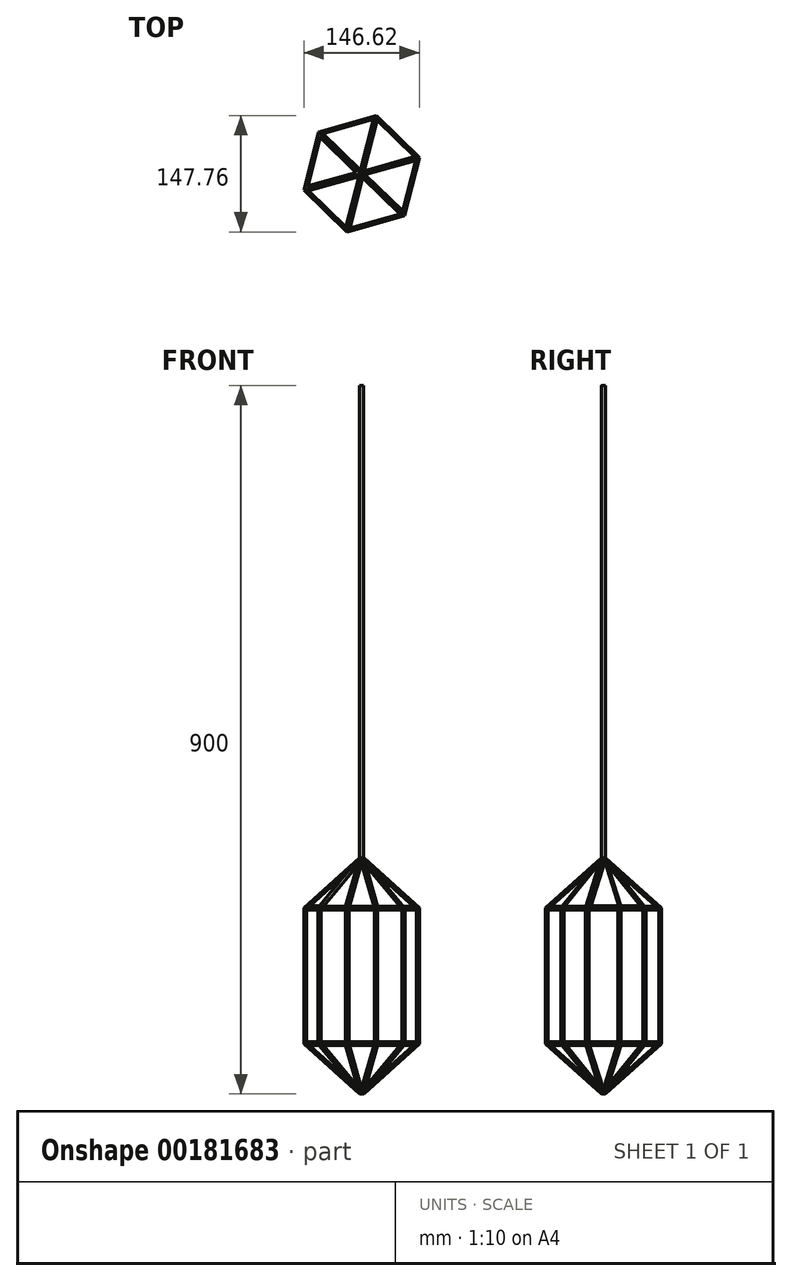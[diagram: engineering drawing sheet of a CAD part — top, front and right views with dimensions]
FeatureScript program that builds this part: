
annotation { "Feature Type Name" : "Feature", "Feature Type Description" : "" }
export const myFeature = defineFeature(function(context is Context, id is Id, definition is map)
    precondition{}
    {
        {
            var Q0;
            Q0=qCreatedBy(makeId("Top.planeOp"),FACE);
            var sketch = newSketch(context, id + "F0", { "sketchPlane" : qUnion([Q0])});
            skCircle(sketch, "E0.cCircle", {"center": v(0, 0) * mm, "radius": 66 * mm, "construction": true});
            skLineSegment(sketch, "E0.0", {"start": v(18.67, 73.88) * mm, "end": v(73.31, 20.77) * mm});
            skLineSegment(sketch, "E0.1", {"start": v(73.31, 20.77) * mm, "end": v(54.65, -53.1) * mm});
            skLineSegment(sketch, "E0.2", {"start": v(54.65, -53.1) * mm, "end": v(-18.67, -73.88) * mm});
            skLineSegment(sketch, "E0.3", {"start": v(-18.67, -73.88) * mm, "end": v(-73.31, -20.77) * mm});
            skLineSegment(sketch, "E0.4", {"start": v(-73.31, -20.77) * mm, "end": v(-54.65, 53.1) * mm});
            skLineSegment(sketch, "E0.5", {"start": v(-54.65, 53.1) * mm, "end": v(18.67, 73.88) * mm});
            skPoint(sketch, "E0.0.midPoint", {"position": v(45.99, 47.33) * mm});
            skSolve(sketch);
        }
        {
            var Q0;
            Q0 = qSketchRegion(id + "F0", true);
            extrude(context, id + "F1", {"entities" : qUnion([Q0]), "depth" : 300 * mm});
        }
        {
            var Q0;
            Q0=makeQuery(id+"F1.opExtrude","CAP_FACE",FACE,{"disambiguationData":[OSD([sQuery(id+"F0.wireOp",EDGE,"E0.0"),sQuery(id+"F0.wireOp",EDGE,"E0.1"),sQuery(id+"F0.wireOp",EDGE,"E0.2"),sQuery(id+"F0.wireOp",EDGE,"E0.3"),sQuery(id+"F0.wireOp",EDGE,"E0.4"),sQuery(id+"F0.wireOp",EDGE,"E0.5")])],"isStart":false});
            var Q1;
            Q1=makeQuery(id+"F1.opExtrude","CAP_FACE",FACE,{"disambiguationData":[OSD([sQuery(id+"F0.wireOp",EDGE,"E0.0"),sQuery(id+"F0.wireOp",EDGE,"E0.1"),sQuery(id+"F0.wireOp",EDGE,"E0.2"),sQuery(id+"F0.wireOp",EDGE,"E0.3"),sQuery(id+"F0.wireOp",EDGE,"E0.4"),sQuery(id+"F0.wireOp",EDGE,"E0.5")])],"isStart":true});
            chamfer(context, id + "F2", {"entities" : qUnion([Q0, Q1]), "width" : 63.5 * mm, "tangentPropagation" : true});
        }
        {
            var Q0;
            {var subQ0=sQuery(id+"F0.wireOp",EDGE,"E0.4");Q0=makeQuery(id+"F2.opChamfer","BLEND_FACE",FACE,{"disambiguationData":[OSD([subQ0]),TDD([makeQuery(id+"F1.opExtrude","CAP_EDGE",EDGE,{"disambiguationData":[OSD([subQ0])],"isStart":false})])]});}
            var Q1;
            Q1=makeQuery(id+"F1.opExtrude","SWEPT_BODY",BODY,{"disambiguationData":[OSD([sQuery(id+"F0.wireOp",EDGE,"E0.0"),sQuery(id+"F0.wireOp",EDGE,"E0.1"),sQuery(id+"F0.wireOp",EDGE,"E0.2"),sQuery(id+"F0.wireOp",EDGE,"E0.3"),sQuery(id+"F0.wireOp",EDGE,"E0.4"),sQuery(id+"F0.wireOp",EDGE,"E0.5")])]});
            shell(context, id + "F3", {"entities" : qUnion([Q0]), "parts" : qUnion([Q1]), "thickness" : 2.54 * mm});
        }
        {
            var Q0;
            {var subQ0=sQuery(id+"F0.wireOp",EDGE,"E0.3");Q0=makeQuery(id+"F2.opChamfer","BLEND_FACE",FACE,{"disambiguationData":[OSD([subQ0]),TDD([makeQuery(id+"F1.opExtrude","CAP_EDGE",EDGE,{"disambiguationData":[OSD([subQ0])],"isStart":false})])]});}
            var sketch = newSketch(context, id + "F4", { "sketchPlane" : qUnion([Q0])});
            skLineSegment(sketch, "E1.0.0", {"start": v(99.68, 77.8) * mm, "end": v(120.32, 172.57) * mm});
            skLineSegment(sketch, "E1.0.1", {"start": v(120.32, 172.57) * mm, "end": v(117.95, 174.2) * mm});
            skLineSegment(sketch, "E1.0.2", {"start": v(36.88, 120.95) * mm, "end": v(117.95, 174.2) * mm});
            skLineSegment(sketch, "E1.0.3", {"start": v(36.88, 120.95) * mm, "end": v(99.68, 77.8) * mm});
            skLineSegment(sketch, "E2.0", {"start": v(98, 82.03) * mm, "end": v(117.33, 170.75) * mm});
            skLineSegment(sketch, "E2.1", {"start": v(41.43, 120.9) * mm, "end": v(98, 82.03) * mm});
            skLineSegment(sketch, "E2.2", {"start": v(41.43, 120.9) * mm, "end": v(117.33, 170.75) * mm});
            skSolve(sketch);
        }
        {
            var Q0;
            Q0=makeQuery(id+"F4.imprint","IMPRINT",FACE,{"disambiguationData":[TD([[makeQuery(id+"F4.imprint","IMPRINT",EDGE,{"derivedFrom":sQuery(id+"F4.wireOp",EDGE,"E2.0")}),1.0]])]});
            extrude(context, id + "F5", {"entities" : qUnion([Q0]), "operationType" : NewBodyOperationType.REMOVE, "endBound" : BoundingType.UP_TO_NEXT, "oppositeDirection" : true, "depth" : 25.4 * mm});
        }
        {
            var Q0;
            {var subQ0=sQuery(id+"F0.wireOp",EDGE,"E0.2");Q0=makeQuery(id+"F2.opChamfer","BLEND_FACE",FACE,{"disambiguationData":[OSD([subQ0]),TDD([makeQuery(id+"F1.opExtrude","CAP_EDGE",EDGE,{"disambiguationData":[OSD([subQ0])],"isStart":false})])]});}
            var sketch = newSketch(context, id + "F6", { "sketchPlane" : qUnion([Q0])});
            skLineSegment(sketch, "E3.0.0", {"start": v(13.67, 125.7) * mm, "end": v(-39.92, 206.55) * mm});
            skLineSegment(sketch, "E3.0.1", {"start": v(-39.92, 206.55) * mm, "end": v(-42.74, 205.99) * mm});
            skLineSegment(sketch, "E3.0.2", {"start": v(-61.04, 110.73) * mm, "end": v(-42.74, 205.99) * mm});
            skLineSegment(sketch, "E3.0.3", {"start": v(-61.04, 110.73) * mm, "end": v(13.67, 125.7) * mm});
            skLineSegment(sketch, "E4.0", {"start": v(9.46, 127.45) * mm, "end": v(-40.7, 203.14) * mm});
            skLineSegment(sketch, "E4.1", {"start": v(-57.84, 113.97) * mm, "end": v(9.46, 127.45) * mm});
            skLineSegment(sketch, "E4.2", {"start": v(-57.84, 113.97) * mm, "end": v(-40.7, 203.14) * mm});
            skSolve(sketch);
        }
        {
            var Q0;
            Q0=makeQuery(id+"F6.imprint","IMPRINT",FACE,{"disambiguationData":[TD([[makeQuery(id+"F6.imprint","IMPRINT",EDGE,{"derivedFrom":sQuery(id+"F6.wireOp",EDGE,"E4.0")}),1.0]])]});
            extrude(context, id + "F7", {"entities" : qUnion([Q0]), "operationType" : NewBodyOperationType.REMOVE, "endBound" : BoundingType.UP_TO_NEXT, "oppositeDirection" : true, "depth" : 25.4 * mm});
        }
        {
            var Q0;
            {var subQ0=sQuery(id+"F0.wireOp",EDGE,"E0.1");Q0=makeQuery(id+"F2.opChamfer","BLEND_FACE",FACE,{"disambiguationData":[OSD([subQ0]),TDD([makeQuery(id+"F1.opExtrude","CAP_EDGE",EDGE,{"disambiguationData":[OSD([subQ0])],"isStart":false})])]});}
            var sketch = newSketch(context, id + "F8", { "sketchPlane" : qUnion([Q0])});
            skLineSegment(sketch, "E5.0.0", {"start": v(-198.59, 69.43) * mm, "end": v(-126.36, 4.69) * mm});
            skLineSegment(sketch, "E5.0.1", {"start": v(-126.36, 4.69) * mm, "end": v(-100.72, 76.45) * mm});
            skLineSegment(sketch, "E5.0.2", {"start": v(-100.72, 76.45) * mm, "end": v(-197.62, 72.14) * mm});
            skLineSegment(sketch, "E5.0.3", {"start": v(-197.62, 72.14) * mm, "end": v(-198.59, 69.43) * mm});
            skLineSegment(sketch, "E6.0", {"start": v(-195.1, 69.7) * mm, "end": v(-127.48, 9.1) * mm});
            skLineSegment(sketch, "E6.1", {"start": v(-104.38, 73.74) * mm, "end": v(-195.1, 69.7) * mm});
            skLineSegment(sketch, "E6.2", {"start": v(-127.48, 9.1) * mm, "end": v(-104.38, 73.74) * mm});
            skSolve(sketch);
        }
        {
            var Q0;
            Q0 = qSketchRegion(id + "F8", true);
            var Q1;
            {var subQ0=sQuery(id+"F8.wireOp",EDGE,"144117f5-ceeb-445f-adcc-b0d1e90e878f.3");Q1=makeQuery(id+"F8.imprint","IMPRINT",FACE,{"disambiguationData":[TD([[makeQuery(id+"F8.imprint","IMPRINT",EDGE,{"derivedFrom":subQ0}),1.0]])]});}
            extrude(context, id + "F9", {"entities" : qUnion([Q0, Q1]), "operationType" : NewBodyOperationType.REMOVE, "endBound" : BoundingType.UP_TO_NEXT, "oppositeDirection" : true, "depth" : 25.4 * mm});
        }
        {
            var Q0;
            Q0 = qSketchRegion(id + "F8", true);
            var Q1;
            {var subQ0=sQuery(id+"F0.wireOp",EDGE,"E0.1");Q1=makeQuery(id+"F2.opChamfer","BLEND_FACE",FACE,{"disambiguationData":[OSD([subQ0]),TDD([makeQuery(id+"F1.opExtrude","CAP_EDGE",EDGE,{"disambiguationData":[OSD([subQ0])],"isStart":false})])]});}
            extrude(context, id + "F10", {"entities" : qUnion([Q0, Q1]), "operationType" : NewBodyOperationType.REMOVE, "endBound" : BoundingType.UP_TO_NEXT, "oppositeDirection" : true, "depth" : 25.4 * mm});
        }
        {
            var Q0;
            {var subQ0=sQuery(id+"F0.wireOp",EDGE,"E0.0");Q0=makeQuery(id+"F2.opChamfer","BLEND_FACE",FACE,{"disambiguationData":[OSD([subQ0]),TDD([makeQuery(id+"F1.opExtrude","CAP_EDGE",EDGE,{"disambiguationData":[OSD([subQ0])],"isStart":false})])]});}
            var sketch = newSketch(context, id + "F11", { "sketchPlane" : qUnion([Q0])});
            skLineSegment(sketch, "E7.0.0", {"start": v(-117.95, -174.2) * mm, "end": v(-36.88, -120.95) * mm});
            skLineSegment(sketch, "E7.0.1", {"start": v(-36.88, -120.95) * mm, "end": v(-99.68, -77.8) * mm});
            skLineSegment(sketch, "E7.0.2", {"start": v(-120.32, -172.57) * mm, "end": v(-99.68, -77.8) * mm});
            skLineSegment(sketch, "E7.0.3", {"start": v(-120.32, -172.57) * mm, "end": v(-117.95, -174.2) * mm});
            skLineSegment(sketch, "E8.0", {"start": v(-117.33, -170.75) * mm, "end": v(-98, -82.03) * mm});
            skLineSegment(sketch, "E8.1", {"start": v(-117.33, -170.75) * mm, "end": v(-41.43, -120.9) * mm});
            skLineSegment(sketch, "E8.2", {"start": v(-41.43, -120.9) * mm, "end": v(-98, -82.03) * mm});
            skSolve(sketch);
        }
        {
            var Q0;
            Q0=makeQuery(id+"F11.imprint","IMPRINT",FACE,{"disambiguationData":[TD([[makeQuery(id+"F11.imprint","IMPRINT",EDGE,{"derivedFrom":sQuery(id+"F11.wireOp",EDGE,"E8.0")}),-1.0]])]});
            extrude(context, id + "F12", {"entities" : qUnion([Q0]), "operationType" : NewBodyOperationType.REMOVE, "endBound" : BoundingType.UP_TO_NEXT, "oppositeDirection" : true, "depth" : 25.4 * mm});
        }
        {
            var Q0;
            {var subQ0=sQuery(id+"F0.wireOp",EDGE,"E0.5");Q0=makeQuery(id+"F2.opChamfer","BLEND_FACE",FACE,{"disambiguationData":[OSD([subQ0]),TDD([makeQuery(id+"F1.opExtrude","CAP_EDGE",EDGE,{"disambiguationData":[OSD([subQ0])],"isStart":false})])]});}
            var sketch = newSketch(context, id + "F13", { "sketchPlane" : qUnion([Q0])});
            skLineSegment(sketch, "E9.0.0", {"start": v(-13.67, -125.7) * mm, "end": v(39.92, -206.55) * mm});
            skLineSegment(sketch, "E9.0.1", {"start": v(39.92, -206.55) * mm, "end": v(42.74, -205.99) * mm});
            skLineSegment(sketch, "E9.0.2", {"start": v(42.74, -205.99) * mm, "end": v(61.04, -110.73) * mm});
            skLineSegment(sketch, "E9.0.3", {"start": v(61.04, -110.73) * mm, "end": v(-13.67, -125.7) * mm});
            skLineSegment(sketch, "E10.0", {"start": v(-9.46, -127.45) * mm, "end": v(40.7, -203.14) * mm});
            skLineSegment(sketch, "E10.1", {"start": v(57.84, -113.97) * mm, "end": v(-9.46, -127.45) * mm});
            skLineSegment(sketch, "E10.2", {"start": v(40.7, -203.14) * mm, "end": v(57.84, -113.97) * mm});
            skSolve(sketch);
        }
        {
            var Q0;
            Q0=makeQuery(id+"F13.imprint","IMPRINT",FACE,{"disambiguationData":[TD([[makeQuery(id+"F13.imprint","IMPRINT",EDGE,{"derivedFrom":sQuery(id+"F13.wireOp",EDGE,"E10.0")}),1.0]])]});
            extrude(context, id + "F14", {"entities" : qUnion([Q0]), "operationType" : NewBodyOperationType.REMOVE, "endBound" : BoundingType.UP_TO_NEXT, "oppositeDirection" : true, "depth" : 25.4 * mm});
        }
        {
            var Q0;
            Q0=makeQuery(id+"F1.opExtrude","SWEPT_FACE",FACE,{"disambiguationData":[OSD([sQuery(id+"F0.wireOp",EDGE,"E0.2")])]});
            var sketch = newSketch(context, id + "F15", { "sketchPlane" : qUnion([Q0])});
            skLineSegment(sketch, "E11.0.0", {"start": v(-38.1, 236.5) * mm, "end": v(-38.1, 63.5) * mm});
            skLineSegment(sketch, "E11.0.1", {"start": v(-38.1, 63.5) * mm, "end": v(38.1, 63.5) * mm});
            skLineSegment(sketch, "E11.0.2", {"start": v(38.1, 63.5) * mm, "end": v(38.1, 236.5) * mm});
            skLineSegment(sketch, "E11.0.3", {"start": v(38.1, 236.5) * mm, "end": v(-38.1, 236.5) * mm});
            skLineSegment(sketch, "E12.0", {"start": v(-35.56, 233.96) * mm, "end": v(-35.56, 66.04) * mm});
            skLineSegment(sketch, "E12.1", {"start": v(35.56, 233.96) * mm, "end": v(-35.56, 233.96) * mm});
            skLineSegment(sketch, "E12.2", {"start": v(35.56, 66.04) * mm, "end": v(35.56, 233.96) * mm});
            skLineSegment(sketch, "E12.3", {"start": v(-35.56, 66.04) * mm, "end": v(35.56, 66.04) * mm});
            skSolve(sketch);
        }
        {
            var Q0;
            Q0=makeQuery(id+"F15.imprint","IMPRINT",FACE,{"disambiguationData":[TD([[makeQuery(id+"F15.imprint","IMPRINT",EDGE,{"derivedFrom":sQuery(id+"F15.wireOp",EDGE,"E12.0")}),1.0]])]});
            extrude(context, id + "F16", {"entities" : qUnion([Q0]), "operationType" : NewBodyOperationType.REMOVE, "endBound" : BoundingType.THROUGH_ALL, "oppositeDirection" : true, "depth" : 25.4 * mm});
        }
        {
            var Q0;
            Q0=makeQuery(id+"F1.opExtrude","SWEPT_FACE",FACE,{"disambiguationData":[OSD([sQuery(id+"F0.wireOp",EDGE,"E0.1")])]});
            var sketch = newSketch(context, id + "F17", { "sketchPlane" : qUnion([Q0])});
            skLineSegment(sketch, "E13.0.0", {"start": v(-38.1, 236.5) * mm, "end": v(-38.1, 63.5) * mm});
            skLineSegment(sketch, "E13.0.1", {"start": v(-38.1, 63.5) * mm, "end": v(38.1, 63.5) * mm});
            skLineSegment(sketch, "E13.0.2", {"start": v(38.1, 63.5) * mm, "end": v(38.1, 236.5) * mm});
            skLineSegment(sketch, "E13.0.3", {"start": v(38.1, 236.5) * mm, "end": v(-38.1, 236.5) * mm});
            skLineSegment(sketch, "E14.0", {"start": v(35.56, 233.96) * mm, "end": v(-35.56, 233.96) * mm});
            skLineSegment(sketch, "E14.1", {"start": v(35.56, 66.04) * mm, "end": v(35.56, 233.96) * mm});
            skLineSegment(sketch, "E14.2", {"start": v(-35.56, 66.04) * mm, "end": v(35.56, 66.04) * mm});
            skLineSegment(sketch, "E14.3", {"start": v(-35.56, 233.96) * mm, "end": v(-35.56, 66.04) * mm});
            skSolve(sketch);
        }
        {
            var Q0;
            Q0=makeQuery(id+"F17.imprint","IMPRINT",FACE,{"disambiguationData":[TD([[makeQuery(id+"F17.imprint","IMPRINT",EDGE,{"derivedFrom":sQuery(id+"F17.wireOp",EDGE,"E14.0")}),1.0]])]});
            extrude(context, id + "F18", {"entities" : qUnion([Q0]), "operationType" : NewBodyOperationType.REMOVE, "endBound" : BoundingType.THROUGH_ALL, "oppositeDirection" : true, "depth" : 25.4 * mm});
        }
        {
            var Q0;
            Q0=makeQuery(id+"F1.opExtrude","SWEPT_FACE",FACE,{"disambiguationData":[OSD([sQuery(id+"F0.wireOp",EDGE,"E0.0")])]});
            var sketch = newSketch(context, id + "F19", { "sketchPlane" : qUnion([Q0])});
            skLineSegment(sketch, "E15.0.0", {"start": v(-38.1, 236.5) * mm, "end": v(-38.1, 63.5) * mm});
            skLineSegment(sketch, "E15.0.1", {"start": v(-38.1, 63.5) * mm, "end": v(38.1, 63.5) * mm});
            skLineSegment(sketch, "E15.0.2", {"start": v(38.1, 63.5) * mm, "end": v(38.1, 236.5) * mm});
            skLineSegment(sketch, "E15.0.3", {"start": v(38.1, 236.5) * mm, "end": v(-38.1, 236.5) * mm});
            skLineSegment(sketch, "E16.0", {"start": v(35.56, 233.96) * mm, "end": v(-35.56, 233.96) * mm});
            skLineSegment(sketch, "E16.1", {"start": v(35.56, 66.04) * mm, "end": v(35.56, 233.96) * mm});
            skLineSegment(sketch, "E16.2", {"start": v(-35.56, 66.04) * mm, "end": v(35.56, 66.04) * mm});
            skLineSegment(sketch, "E16.3", {"start": v(-35.56, 233.96) * mm, "end": v(-35.56, 66.04) * mm});
            skSolve(sketch);
        }
        {
            var Q0;
            Q0=makeQuery(id+"F19.imprint","IMPRINT",FACE,{"disambiguationData":[TD([[makeQuery(id+"F19.imprint","IMPRINT",EDGE,{"derivedFrom":sQuery(id+"F19.wireOp",EDGE,"E16.0")}),1.0]])]});
            extrude(context, id + "F20", {"entities" : qUnion([Q0]), "operationType" : NewBodyOperationType.REMOVE, "endBound" : BoundingType.THROUGH_ALL, "oppositeDirection" : true, "depth" : 25.4 * mm});
        }
        {
            var Q0;
            {var subQ0=sQuery(id+"F0.wireOp",EDGE,"E0.1");Q0=makeQuery(id+"F2.opChamfer","BLEND_FACE",FACE,{"disambiguationData":[OSD([subQ0]),TDD([makeQuery(id+"F1.opExtrude","CAP_EDGE",EDGE,{"disambiguationData":[OSD([subQ0])],"isStart":true})])]});}
            var sketch = newSketch(context, id + "F21", { "sketchPlane" : qUnion([Q0])});
            skLineSegment(sketch, "E17.0.0", {"start": v(73.4, 66.69) * mm, "end": v(1.17, 1.95) * mm});
            skLineSegment(sketch, "E17.0.1", {"start": v(1.17, 1.95) * mm, "end": v(2.14, -0.76) * mm});
            skLineSegment(sketch, "E17.0.2", {"start": v(2.14, -0.76) * mm, "end": v(99.04, -5.07) * mm});
            skLineSegment(sketch, "E17.0.3", {"start": v(99.04, -5.07) * mm, "end": v(73.4, 66.69) * mm});
            skLineSegment(sketch, "E18.0", {"start": v(72.29, 62.27) * mm, "end": v(4.67, 1.67) * mm});
            skLineSegment(sketch, "E18.1", {"start": v(95.38, -2.36) * mm, "end": v(72.29, 62.27) * mm});
            skLineSegment(sketch, "E18.2", {"start": v(4.67, 1.67) * mm, "end": v(95.38, -2.36) * mm});
            skLineSegment(sketch, "E19.0", {"start": v(76.2, 77.72) * mm, "end": v(-6.24, 3.83) * mm});
            skLineSegment(sketch, "E19.1", {"start": v(108.2, -11.83) * mm, "end": v(76.2, 77.72) * mm});
            skLineSegment(sketch, "E19.2", {"start": v(-2.4, -6.92) * mm, "end": v(108.2, -11.83) * mm});
            skLineSegment(sketch, "E19.3", {"start": v(-6.24, 3.83) * mm, "end": v(-2.4, -6.92) * mm});
            skSolve(sketch);
        }
        {
            var Q0;
            Q0=makeQuery(id+"F21.imprint","IMPRINT",FACE,{"disambiguationData":[TD([[makeQuery(id+"F21.imprint","IMPRINT",EDGE,{"derivedFrom":sQuery(id+"F21.wireOp",EDGE,"E18.0")}),1.0]])]});
            extrude(context, id + "F22", {"entities" : qUnion([Q0]), "operationType" : NewBodyOperationType.REMOVE, "endBound" : BoundingType.UP_TO_NEXT, "oppositeDirection" : true, "depth" : 25.4 * mm});
        }
        {
            var Q0;
            {var subQ0=sQuery(id+"F0.wireOp",EDGE,"E0.0");Q0=makeQuery(id+"F2.opChamfer","BLEND_FACE",FACE,{"disambiguationData":[OSD([subQ0]),TDD([makeQuery(id+"F1.opExtrude","CAP_EDGE",EDGE,{"disambiguationData":[OSD([subQ0])],"isStart":true})])]});}
            var sketch = newSketch(context, id + "F23", { "sketchPlane" : qUnion([Q0])});
            skLineSegment(sketch, "E20.0.0", {"start": v(83.26, -53.89) * mm, "end": v(2.18, -0.64) * mm});
            skLineSegment(sketch, "E20.0.1", {"start": v(2.18, -0.64) * mm, "end": v(-0.19, -2.27) * mm});
            skLineSegment(sketch, "E20.0.2", {"start": v(20.45, -97.04) * mm, "end": v(-0.19, -2.27) * mm});
            skLineSegment(sketch, "E20.0.3", {"start": v(20.45, -97.04) * mm, "end": v(83.26, -53.89) * mm});
            skLineSegment(sketch, "E21.0", {"start": v(78.7, -53.94) * mm, "end": v(2.8, -4.09) * mm});
            skLineSegment(sketch, "E21.1", {"start": v(22.13, -92.8) * mm, "end": v(78.7, -53.94) * mm});
            skLineSegment(sketch, "E21.2", {"start": v(22.13, -92.8) * mm, "end": v(2.8, -4.09) * mm});
            skSolve(sketch);
        }
        {
            var Q0;
            Q0=makeQuery(id+"F23.imprint","IMPRINT",FACE,{"disambiguationData":[TD([[makeQuery(id+"F23.imprint","IMPRINT",EDGE,{"derivedFrom":sQuery(id+"F23.wireOp",EDGE,"E21.0")}),1.0]])]});
            extrude(context, id + "F24", {"entities" : qUnion([Q0]), "operationType" : NewBodyOperationType.REMOVE, "endBound" : BoundingType.UP_TO_NEXT, "oppositeDirection" : true, "depth" : 25.4 * mm});
        }
        {
            var Q0;
            {var subQ0=sQuery(id+"F0.wireOp",EDGE,"E0.5");Q0=makeQuery(id+"F2.opChamfer","BLEND_FACE",FACE,{"disambiguationData":[OSD([subQ0]),TDD([makeQuery(id+"F1.opExtrude","CAP_EDGE",EDGE,{"disambiguationData":[OSD([subQ0])],"isStart":true})])]});}
            var sketch = newSketch(context, id + "F25", { "sketchPlane" : qUnion([Q0])});
            skLineSegment(sketch, "E22.0.0", {"start": v(-1.76, -1.44) * mm, "end": v(-55.35, -82.3) * mm});
            skLineSegment(sketch, "E22.0.1", {"start": v(-55.35, -82.3) * mm, "end": v(19.37, -97.26) * mm});
            skLineSegment(sketch, "E22.0.2", {"start": v(19.37, -97.26) * mm, "end": v(1.06, -2) * mm});
            skLineSegment(sketch, "E22.0.3", {"start": v(1.06, -2) * mm, "end": v(-1.76, -1.44) * mm});
            skLineSegment(sketch, "E23.0", {"start": v(-0.97, -4.86) * mm, "end": v(-51.14, -80.55) * mm});
            skLineSegment(sketch, "E23.1", {"start": v(16.16, -94.03) * mm, "end": v(-0.97, -4.86) * mm});
            skLineSegment(sketch, "E23.2", {"start": v(-51.14, -80.55) * mm, "end": v(16.16, -94.03) * mm});
            skLineSegment(sketch, "E24.0", {"start": v(-4.7, 5.62) * mm, "end": v(-65.86, -86.66) * mm});
            skLineSegment(sketch, "E24.1", {"start": v(6.5, 3.38) * mm, "end": v(-4.7, 5.62) * mm});
            skLineSegment(sketch, "E24.2", {"start": v(27.39, -105.35) * mm, "end": v(6.5, 3.38) * mm});
            skLineSegment(sketch, "E24.3", {"start": v(-65.86, -86.66) * mm, "end": v(27.39, -105.35) * mm});
            skSolve(sketch);
        }
        {
            var Q0;
            Q0=makeQuery(id+"F25.imprint","IMPRINT",FACE,{"disambiguationData":[TD([[makeQuery(id+"F25.imprint","IMPRINT",EDGE,{"derivedFrom":sQuery(id+"F25.wireOp",EDGE,"E23.0")}),1.0]])]});
            extrude(context, id + "F26", {"entities" : qUnion([Q0]), "operationType" : NewBodyOperationType.REMOVE, "endBound" : BoundingType.UP_TO_NEXT, "oppositeDirection" : true, "depth" : 25.4 * mm});
        }
        {
            var Q0;
            {var subQ0=sQuery(id+"F0.wireOp",EDGE,"E0.4");Q0=makeQuery(id+"F2.opChamfer","BLEND_FACE",FACE,{"disambiguationData":[OSD([subQ0]),TDD([makeQuery(id+"F1.opExtrude","CAP_EDGE",EDGE,{"disambiguationData":[OSD([subQ0])],"isStart":true})])]});}
            var sketch = newSketch(context, id + "F27", { "sketchPlane" : qUnion([Q0])});
            skLineSegment(sketch, "E25.0.0", {"start": v(-2.14, 0.76) * mm, "end": v(-99.04, 5.07) * mm});
            skLineSegment(sketch, "E25.0.1", {"start": v(-99.04, 5.07) * mm, "end": v(-73.4, -66.69) * mm});
            skLineSegment(sketch, "E25.0.2", {"start": v(-1.17, -1.95) * mm, "end": v(-73.4, -66.69) * mm});
            skLineSegment(sketch, "E25.0.3", {"start": v(-1.17, -1.95) * mm, "end": v(-2.14, 0.76) * mm});
            skLineSegment(sketch, "E26.0", {"start": v(-4.67, -1.67) * mm, "end": v(-95.38, 2.36) * mm});
            skLineSegment(sketch, "E26.1", {"start": v(-4.67, -1.67) * mm, "end": v(-72.29, -62.27) * mm});
            skLineSegment(sketch, "E26.2", {"start": v(-95.38, 2.36) * mm, "end": v(-72.29, -62.27) * mm});
            skSolve(sketch);
        }
        {
            var Q0;
            Q0=makeQuery(id+"F27.imprint","IMPRINT",FACE,{"disambiguationData":[TD([[makeQuery(id+"F27.imprint","IMPRINT",EDGE,{"derivedFrom":sQuery(id+"F27.wireOp",EDGE,"E26.0")}),1.0]])]});
            extrude(context, id + "F28", {"entities" : qUnion([Q0]), "operationType" : NewBodyOperationType.REMOVE, "endBound" : BoundingType.UP_TO_NEXT, "oppositeDirection" : true, "depth" : 25.4 * mm});
        }
        {
            var Q0;
            {var subQ0=sQuery(id+"F0.wireOp",EDGE,"E0.3");Q0=makeQuery(id+"F2.opChamfer","BLEND_FACE",FACE,{"disambiguationData":[OSD([subQ0]),TDD([makeQuery(id+"F1.opExtrude","CAP_EDGE",EDGE,{"disambiguationData":[OSD([subQ0])],"isStart":true})])]});}
            var sketch = newSketch(context, id + "F29", { "sketchPlane" : qUnion([Q0])});
            skLineSegment(sketch, "E27.0.0", {"start": v(0.19, 2.27) * mm, "end": v(-20.45, 97.04) * mm});
            skLineSegment(sketch, "E27.0.1", {"start": v(-20.45, 97.04) * mm, "end": v(-83.26, 53.89) * mm});
            skLineSegment(sketch, "E27.0.2", {"start": v(-2.18, 0.64) * mm, "end": v(-83.26, 53.89) * mm});
            skLineSegment(sketch, "E27.0.3", {"start": v(-2.18, 0.64) * mm, "end": v(0.19, 2.27) * mm});
            skLineSegment(sketch, "E28.0", {"start": v(-2.8, 4.09) * mm, "end": v(-22.13, 92.8) * mm});
            skLineSegment(sketch, "E28.1", {"start": v(-2.8, 4.09) * mm, "end": v(-78.7, 53.94) * mm});
            skLineSegment(sketch, "E28.2", {"start": v(-22.13, 92.8) * mm, "end": v(-78.7, 53.94) * mm});
            skSolve(sketch);
        }
        {
            var Q0;
            Q0=makeQuery(id+"F29.imprint","IMPRINT",FACE,{"disambiguationData":[TD([[makeQuery(id+"F29.imprint","IMPRINT",EDGE,{"derivedFrom":sQuery(id+"F29.wireOp",EDGE,"E28.0")}),1.0]])]});
            extrude(context, id + "F30", {"entities" : qUnion([Q0]), "operationType" : NewBodyOperationType.REMOVE, "endBound" : BoundingType.UP_TO_NEXT, "oppositeDirection" : true, "depth" : 25.4 * mm});
        }
        {
            var Q0;
            {var subQ0=sQuery(id+"F0.wireOp",EDGE,"E0.2");Q0=makeQuery(id+"F2.opChamfer","BLEND_FACE",FACE,{"disambiguationData":[OSD([subQ0]),TDD([makeQuery(id+"F1.opExtrude","CAP_EDGE",EDGE,{"disambiguationData":[OSD([subQ0])],"isStart":true})])]});}
            var sketch = newSketch(context, id + "F31", { "sketchPlane" : qUnion([Q0])});
            skLineSegment(sketch, "E29.0.0", {"start": v(1.76, 1.44) * mm, "end": v(55.35, 82.3) * mm});
            skLineSegment(sketch, "E29.0.1", {"start": v(55.35, 82.3) * mm, "end": v(-19.37, 97.26) * mm});
            skLineSegment(sketch, "E29.0.2", {"start": v(-1.06, 2) * mm, "end": v(-19.37, 97.26) * mm});
            skLineSegment(sketch, "E29.0.3", {"start": v(-1.06, 2) * mm, "end": v(1.76, 1.44) * mm});
            skLineSegment(sketch, "E30.0", {"start": v(0.97, 4.86) * mm, "end": v(51.14, 80.55) * mm});
            skLineSegment(sketch, "E30.1", {"start": v(0.97, 4.86) * mm, "end": v(-16.16, 94.03) * mm});
            skLineSegment(sketch, "E30.2", {"start": v(51.14, 80.55) * mm, "end": v(-16.16, 94.03) * mm});
            skSolve(sketch);
        }
        {
            var Q0;
            Q0=makeQuery(id+"F31.imprint","IMPRINT",FACE,{"disambiguationData":[TD([[makeQuery(id+"F31.imprint","IMPRINT",EDGE,{"derivedFrom":sQuery(id+"F31.wireOp",EDGE,"E30.0")}),1.0]])]});
            extrude(context, id + "F32", {"entities" : qUnion([Q0]), "operationType" : NewBodyOperationType.REMOVE, "endBound" : BoundingType.UP_TO_NEXT, "oppositeDirection" : true, "depth" : 25.4 * mm});
        }
        {
            var Q0;
            Q0=makeQuery(id+"F1.opExtrude","CAP_FACE",FACE,{"disambiguationData":[OSD([sQuery(id+"F0.wireOp",EDGE,"E0.0"),sQuery(id+"F0.wireOp",EDGE,"E0.1"),sQuery(id+"F0.wireOp",EDGE,"E0.2"),sQuery(id+"F0.wireOp",EDGE,"E0.3"),sQuery(id+"F0.wireOp",EDGE,"E0.4"),sQuery(id+"F0.wireOp",EDGE,"E0.5")])],"isStart":false});
            var sketch = newSketch(context, id + "F33", { "sketchPlane" : qUnion([Q0])});
            skCircle(sketch, "E31", {"center": v(0, 0) * mm, "radius": 2.5 * mm});
            skSolve(sketch);
        }
        {
            var Q0;
            Q0 = qSketchRegion(id + "F33", true);
            extrude(context, id + "F34", {"entities" : qUnion([Q0]), "operationType" : NewBodyOperationType.ADD, "depth" : 600 * mm});
        }
    });
